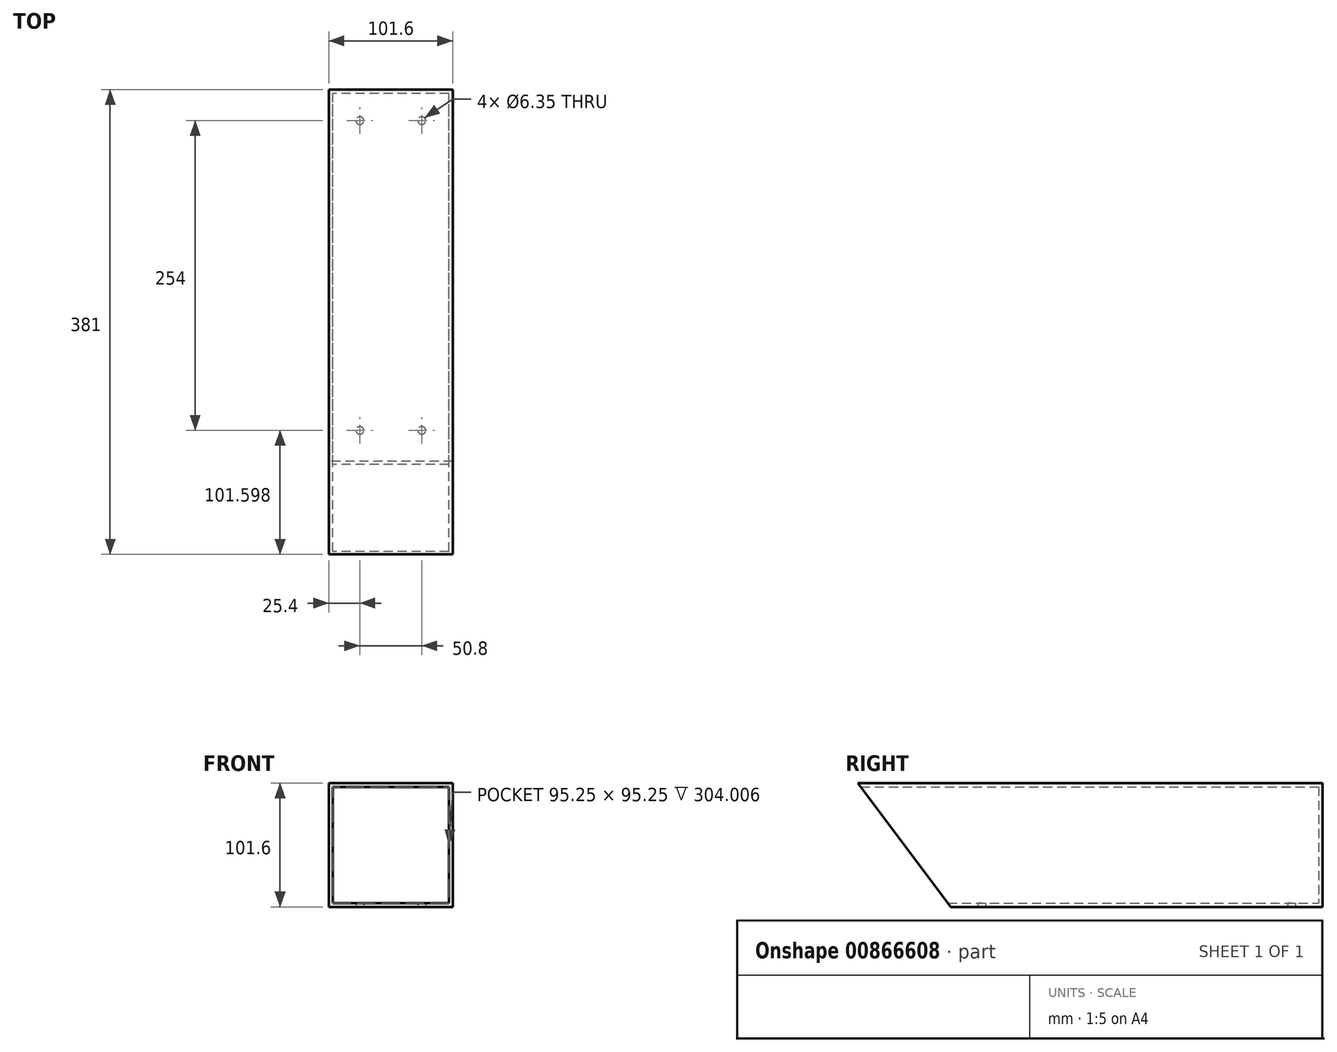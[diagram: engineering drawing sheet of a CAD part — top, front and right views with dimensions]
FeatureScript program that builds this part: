
annotation { "Feature Type Name" : "Feature", "Feature Type Description" : "" }
export const myFeature = defineFeature(function(context is Context, id is Id, definition is map)
    precondition{}
    {
        {
            var Q0;
            Q0=qCreatedBy(makeId("Right.planeOp"),FACE);
            var sketch = newSketch(context, id + "F0", { "sketchPlane" : qUnion([Q0])});
            skLineSegment(sketch, "E0.bottom", {"start": v(-195.57, -23.16) * mm, "end": v(185.43, -23.16) * mm});
            skLineSegment(sketch, "E0.right", {"start": v(185.43, -23.16) * mm, "end": v(185.43, -124.76) * mm});
            skLineSegment(sketch, "E1", {"start": v(-195.57, -23.16) * mm, "end": v(-119.37, -124.76) * mm});
            skLineSegment(sketch, "E2", {"start": v(-119.37, -124.76) * mm, "end": v(185.43, -124.76) * mm});
            skSolve(sketch);
        }
        {
            var Q0;
            Q0=makeQuery(id+"F0.imprint","IMPRINT",FACE,{"disambiguationData":[TD([[makeQuery(id+"F0.imprint","IMPRINT",EDGE,{"derivedFrom":sQuery(id+"F0.wireOp",EDGE,"E0.bottom")}),-1.0]])]});
            extrude(context, id + "F1", {"entities" : qUnion([Q0]), "depth" : 101.6 * mm, "offsetDistance" : 25.4 * mm});
        }
        {
            var Q0;
            Q0=makeQuery(id+"F1.opExtrude","SWEPT_FACE",FACE,{"disambiguationData":[OSD([sQuery(id+"F0.wireOp",EDGE,"E1")])]});
            shell(context, id + "F2", {"entities" : qUnion([Q0]), "thickness" : 3.17 * mm});
        }
        {
            var Q0;
            Q0=makeQuery(id+"F1.opExtrude","SWEPT_FACE",FACE,{"disambiguationData":[OSD([sQuery(id+"F0.wireOp",EDGE,"E2")])]});
            var sketch = newSketch(context, id + "F3", { "sketchPlane" : qUnion([Q0])});
            skCircle(sketch, "E3", {"center": v(25.4, 93.97) * mm, "radius": 3.18 * mm});
            skCircle(sketch, "E4", {"center": v(76.2, 93.97) * mm, "radius": 3.18 * mm});
            skCircle(sketch, "E5", {"center": v(25.4, -160.03) * mm, "radius": 3.18 * mm});
            skCircle(sketch, "E6", {"center": v(76.2, -160.03) * mm, "radius": 3.18 * mm});
            skSolve(sketch);
        }
        {
            var Q0;
            Q0=makeQuery(id+"F3.imprint","IMPRINT",FACE,{"disambiguationData":[TD([[makeQuery(id+"F3.imprint","IMPRINT",EDGE,{"derivedFrom":sQuery(id+"F3.wireOp",EDGE,"E3")}),1.0]])]});
            var Q1;
            Q1=makeQuery(id+"F3.imprint","IMPRINT",FACE,{"disambiguationData":[TD([[makeQuery(id+"F3.imprint","IMPRINT",EDGE,{"derivedFrom":sQuery(id+"F3.wireOp",EDGE,"E4")}),1.0]])]});
            var Q2;
            Q2=makeQuery(id+"F3.imprint","IMPRINT",FACE,{"disambiguationData":[TD([[makeQuery(id+"F3.imprint","IMPRINT",EDGE,{"derivedFrom":sQuery(id+"F3.wireOp",EDGE,"E5")}),1.0]])]});
            var Q3;
            Q3=makeQuery(id+"F3.imprint","IMPRINT",FACE,{"disambiguationData":[TD([[makeQuery(id+"F3.imprint","IMPRINT",EDGE,{"derivedFrom":sQuery(id+"F3.wireOp",EDGE,"E6")}),1.0]])]});
            extrude(context, id + "F4", {"entities" : qUnion([Q0, Q1, Q2, Q3]), "operationType" : NewBodyOperationType.REMOVE, "oppositeDirection" : true, "depth" : 25.4 * mm, "offsetDistance" : 25.4 * mm});
        }
    });
